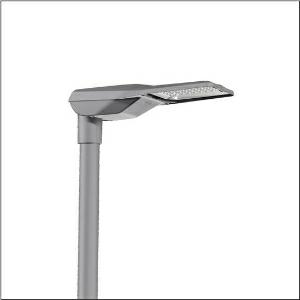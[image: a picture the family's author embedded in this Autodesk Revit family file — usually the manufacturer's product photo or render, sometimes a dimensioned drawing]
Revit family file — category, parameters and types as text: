
# Revit family: streetlight_sl_21_iq_mini___st0_8a_5xe2c31d08hb_f94e
name_source: partatom
category: Lighting Fixtures
units: mm (PartAtom-declared; Revit-internal decimal feet)

## family parameters
Cut with Voids When Loaded = No
Host = Face
Light Source = No
Part Type = Normal
Room Calculation Point = No
Round Connector Dimension = Use Diameter
Shared = No

## types (1)
- --- (1 x LED, 9450 lm, 70.9 W, 3000K)
    Apparent Load = 71 VA
    CIE Flux Codes = 38 75 97 100 100
    Color Rendering = 70
    Color Temperature = 3000K
    Default Elevation = 1800 mm
    Description = Streetlight SL 21 iQ mini, mast luminaire, primary light control with lens, of PMMA, primary optical cover: cover, of toughened safety glass, transparent, light distribution: ST0.8a, light emission: direct distribution, primary light characteristic: asymmetric, installation type: post-top, side-entry, LED, High Power LED, rated luminous flux: 9.450lm, luminous efficacy: 133lm/W, light colour: 730, colour temperature: 3000K, control gear: iQ-Comfort, control: Auto-Match, Temp-Guard, Lumen-Switch, Night-Set, Smart-Wire, Light-Fading, Desk-Remote (wireless, voltage-free reading and setting of iQ features in the workshop via application-optimized NFC function/RFID function), optimised constant luminous flux control (CLO 2.0), pre-setting: linear dimming characteristic, mains connection: 220..240V, AC, 50/60Hz, start of lifetime: 71W, end of service life: 75W, reduction: 31W, luminaire housing, of diecast aluminium, powder-coated, SITECO metallic grey (DB 702S), corrosivity category C5 high according to DIN EN ISO 12944, please order mast flange separately, inclination adjustable: 0°, 5°, 10°, 15°, sealing non-destructively replaceable, multi-level sealing system, length: 628mm, width: 235mm, height: 110mm, mast flange for spigot size: 42mm (side-entry): 5XC10008XM4, 60/48mm (side-entry/post-top): 5XC10108XM2, 76/60mm (side-entry/post-top): 5XC10108XM1, mounting height: 4..8m, protection rating (complete): IP66, insulation class (complete): insulation class II (safety insulation), certification: CE, ENEC, ENEC+, VDE, impact resistance: IK10, permissible operating ambient temperature for outdoor applications: -40..+50°C, standard-compliant lighting for roads and squares, packaging unit: 1 piece

Light Distribution: ST0.8a
    Height = 110 mm
    Lamp = 1 x LED
    Lamp Light Flux = 9450 lm
    Lamp Power = 70.9 W
    Lamp count = 1
    Length = 625 mm
    Luminous efficacy = 133 lm/W
    Manufacturer = Siteco
    ModVariant = No
    Model = 5XE2C31D08HB
    Number of Poles = 1
    OnlyDefault = Yes
    Power Factor = 1
    Product Name = Streetlight SL 21 iQ mini | ST0.8a
    Product group = mast luminaire | pylon top
    ProductGroupID = 6100
    Protection Class = Protection class II
    Protection Degree = IP 66
    RLX_Detail_Level = 1
    RLX_Emergency_Light_Flux = 0 lm
    RLX_Emergency_Type = 0
    RLX_Emergency_Type_DB = No
    RlxData = <blob elided: 26409 chars, md5=34bc50e8>
    Socket = socket
    Standby Power = 0 W
    System Light Flux = 9450 lm
    System Power = 71 W
    Type Comments = factory setting: luminous flux: 100 % | dim-lin: 254 | 711 mA
    Type Image = l_1003519.jpg
    URL = http://relux.com
    VarID = @adj_156919
    Voltage = 0 V
    Weight = 0.00 kg
    Width = 234 mm

## geometry (parser evidence)
native form markers: Blend x4, Sweep x11
no freeform markers — native parametric forms only
